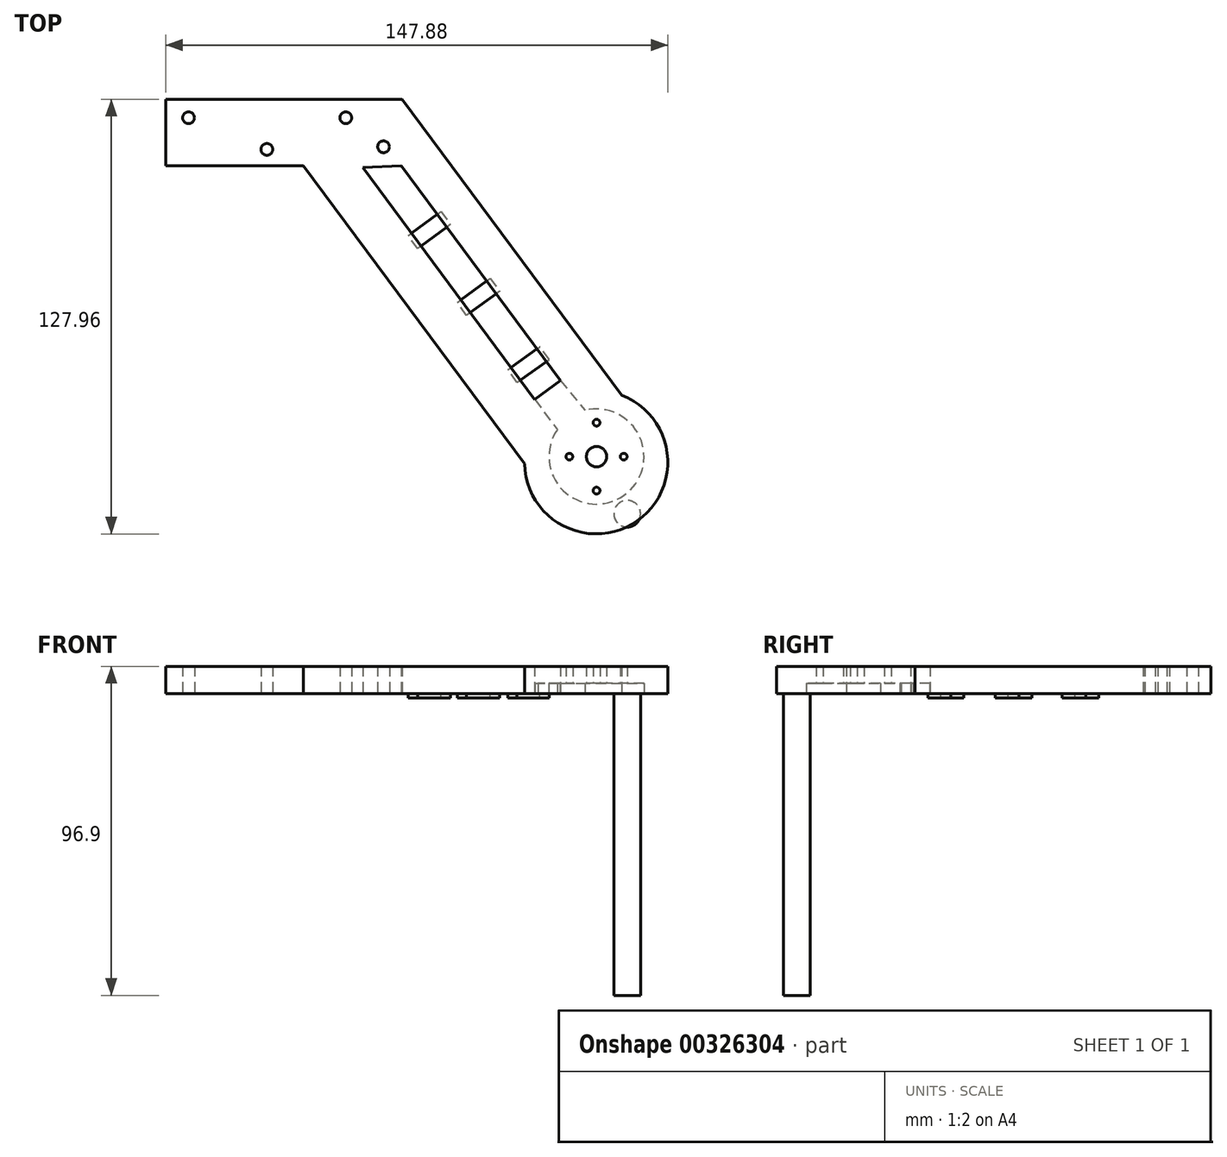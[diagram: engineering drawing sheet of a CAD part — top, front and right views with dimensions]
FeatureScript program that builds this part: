
annotation { "Feature Type Name" : "Feature", "Feature Type Description" : "" }
export const myFeature = defineFeature(function(context is Context, id is Id, definition is map)
    precondition{}
    {
        {
            var Q0;
            Q0=qCreatedBy(makeId("Top.planeOp"),FACE);
            var sketch = newSketch(context, id + "F0", { "sketchPlane" : qUnion([Q0])});
            skLineSegment(sketch, "E0.bottom", {"start": v(0, 0) * mm, "end": v(40.64, 0) * mm});
            skLineSegment(sketch, "E0.top", {"start": v(0, -19.57) * mm, "end": v(40.64, -19.57) * mm});
            skLineSegment(sketch, "E0.left", {"start": v(0, 0) * mm, "end": v(0, -19.57) * mm});
            skLineSegment(sketch, "E0.right", {"start": v(40.64, 0) * mm, "end": v(40.64, -19.57) * mm});
            skLineSegment(sketch, "E1", {"start": v(69.71, 0) * mm, "end": v(40.64, 0) * mm});
            skLineSegment(sketch, "E2", {"start": v(69.71, 0) * mm, "end": v(134.98, -88.06) * mm});
            skLineSegment(sketch, "E3", {"start": v(40.64, -19.57) * mm, "end": v(105.68, -107.31) * mm});
            skLineSegment(sketch, "E4", {"start": v(116.28, -82.77) * mm, "end": v(69.4, -19.51) * mm});
            skLineSegment(sketch, "E5", {"start": v(116.28, -82.77) * mm, "end": v(108.7, -88.39) * mm});
            skLineSegment(sketch, "E6", {"start": v(108.7, -88.39) * mm, "end": v(58.04, -20.03) * mm});
            skLineSegment(sketch, "E7", {"start": v(58.04, -20.03) * mm, "end": v(69.4, -19.51) * mm});
            skCircle(sketch, "E8", {"center": v(126.77, -106.85) * mm, "radius": 21.1 * mm});
            skSolve(sketch);
        }
        {
            var Q0;
            Q0 = qSketchRegion(id + "F0", true);
            extrude(context, id + "F1", {"entities" : qUnion([Q0]), "depth" : 8 * mm});
        }
        {
            var Q0;
            Q0=qCreatedBy(makeId("Top.planeOp"),FACE);
            var sketch = newSketch(context, id + "F2", { "sketchPlane" : qUnion([Q0])});
            skPoint(sketch, "E9.middle", {"position": v(0, 0) * mm});
            skCircle(sketch, "E10", {"center": v(53.08, -5.44) * mm, "radius": 1.73 * mm});
            skCircle(sketch, "E11", {"center": v(6.78, -5.44) * mm, "radius": 1.73 * mm});
            skCircle(sketch, "E12", {"center": v(29.83, -14.74) * mm, "radius": 1.73 * mm});
            skCircle(sketch, "E13", {"center": v(126.9, -105.22) * mm, "radius": 3 * mm});
            skLineSegment(sketch, "E14", {"start": v(126.9, -105.22) * mm, "end": v(126.9, -95.22) * mm});
            skLineSegment(sketch, "E15", {"start": v(118.9, -105.22) * mm, "end": v(126.9, -105.22) * mm});
            skLineSegment(sketch, "E16", {"start": v(126.9, -105.22) * mm, "end": v(134.9, -105.22) * mm});
            skLineSegment(sketch, "E17", {"start": v(126.9, -105.22) * mm, "end": v(126.9, -115.22) * mm});
            skCircle(sketch, "E18", {"center": v(134.9, -105.22) * mm, "radius": 1 * mm});
            skCircle(sketch, "E19", {"center": v(126.9, -115.22) * mm, "radius": 1 * mm});
            skCircle(sketch, "E20", {"center": v(118.9, -105.22) * mm, "radius": 1 * mm});
            skCircle(sketch, "E21", {"center": v(126.9, -95.22) * mm, "radius": 1 * mm});
            skCircle(sketch, "E22", {"center": v(64.19, -13.97) * mm, "radius": 1.73 * mm});
            skSolve(sketch);
        }
        {
            var Q0;
            Q0 = qSketchRegion(id + "F2", true);
            extrude(context, id + "F3", {"entities" : qUnion([Q0]), "operationType" : NewBodyOperationType.REMOVE, "depth" : 101.85 * mm});
        }
        {
            var Q0;
            Q0=qCreatedBy(makeId("Top.planeOp"),FACE);
            var sketch = newSketch(context, id + "F4", { "sketchPlane" : qUnion([Q0])});
            skCircle(sketch, "E23", {"center": v(126.88, -105.2) * mm, "radius": 14 * mm});
            skLineSegment(sketch, "E24", {"start": v(116.27, -82.76) * mm, "end": v(123.75, -91.88) * mm});
            skLineSegment(sketch, "E25", {"start": v(108.73, -88.37) * mm, "end": v(115.64, -97.73) * mm});
            skLineSegment(sketch, "E26", {"start": v(115.64, -97.73) * mm, "end": v(123.75, -91.88) * mm});
            skLineSegment(sketch, "E27", {"start": v(108.73, -88.37) * mm, "end": v(116.27, -82.76) * mm});
            skSolve(sketch);
        }
        {
            var Q0;
            Q0 = qSketchRegion(id + "F4", true);
            extrude(context, id + "F5", {"entities" : qUnion([Q0]), "operationType" : NewBodyOperationType.REMOVE, "depth" : 3 * mm});
        }
        {
            var Q0;
            Q0=qCreatedBy(makeId("Top.planeOp"),FACE);
            var sketch = newSketch(context, id + "F6", { "sketchPlane" : qUnion([Q0])});
            skLineSegment(sketch, "E28", {"start": v(103.49, -83.37) * mm, "end": v(100.8, -79.6) * mm});
            skLineSegment(sketch, "E29", {"start": v(100.8, -79.6) * mm, "end": v(110.23, -72.87) * mm});
            skLineSegment(sketch, "E30", {"start": v(103.49, -83.37) * mm, "end": v(112.92, -76.63) * mm});
            skLineSegment(sketch, "E31", {"start": v(112.92, -76.63) * mm, "end": v(110.23, -72.87) * mm});
            skLineSegment(sketch, "E32", {"start": v(88.64, -63.6) * mm, "end": v(85.87, -59.78) * mm});
            skLineSegment(sketch, "E33", {"start": v(85.87, -59.78) * mm, "end": v(95.61, -52.72) * mm});
            skLineSegment(sketch, "E34", {"start": v(95.61, -52.72) * mm, "end": v(98.38, -56.55) * mm});
            skLineSegment(sketch, "E35", {"start": v(98.38, -56.55) * mm, "end": v(88.64, -63.6) * mm});
            skLineSegment(sketch, "E36", {"start": v(81.1, -33.04) * mm, "end": v(83.88, -36.86) * mm});
            skLineSegment(sketch, "E37", {"start": v(83.88, -36.86) * mm, "end": v(74.25, -43.9) * mm});
            skLineSegment(sketch, "E38", {"start": v(74.25, -43.9) * mm, "end": v(71.46, -40.08) * mm});
            skLineSegment(sketch, "E39", {"start": v(71.46, -40.08) * mm, "end": v(81.1, -33.04) * mm});
            skSolve(sketch);
        }
        {
            var Q0;
            Q0 = qSketchRegion(id + "F6", true);
            extrude(context, id + "F7", {"entities" : qUnion([Q0]), "operationType" : NewBodyOperationType.ADD, "oppositeDirection" : true, "depth" : 1.27 * mm});
        }
        {
            var Q0;
            {var subQ0=makeQuery(id+"F1.opExtrude","CAP_FACE",FACE,{"disambiguationData":[OSD([sQuery(id+"F0.wireOp",EDGE,"E0.bottom"),sQuery(id+"F0.wireOp",EDGE,"E0.top"),sQuery(id+"F0.wireOp",EDGE,"E0.left"),sQuery(id+"F0.wireOp",EDGE,"E1"),sQuery(id+"F0.wireOp",EDGE,"E2"),sQuery(id+"F0.wireOp",EDGE,"E3"),sQuery(id+"F0.wireOp",EDGE,"E4"),sQuery(id+"F0.wireOp",EDGE,"E5"),sQuery(id+"F0.wireOp",EDGE,"E6"),sQuery(id+"F0.wireOp",EDGE,"E7"),sQuery(id+"F0.wireOp",EDGE,"E8")])],"isStart":true});Q0=makeQuery(id+"FJdtKUPKbq1o1Xk_1.boolean.opBoolean","MERGE",FACE,{"derivedFrom":[subQ0,makeQuery(id+"FJdtKUPKbq1o1Xk_1.opPattern","COPY",FACE,{"derivedFrom":subQ0,"instanceName":"1"})]});}
            var sketch = newSketch(context, id + "F8", { "sketchPlane" : qUnion([Q0])});
            skCircle(sketch, "E40", {"center": v(135.92, 122.03) * mm, "radius": 3.93 * mm});
            skSolve(sketch);
        }
        {
            var Q0;
            Q0=makeQuery(id+"F8.imprint","IMPRINT",FACE,{"disambiguationData":[TD([[makeQuery(id+"F8.imprint","IMPRINT",EDGE,{"derivedFrom":sQuery(id+"F8.wireOp",EDGE,"E40")}),1.0]])]});
            extrude(context, id + "F9", {"entities" : qUnion([Q0]), "operationType" : NewBodyOperationType.ADD, "depth" : 88.9 * mm});
        }
    });
